# Revit family: Diverter-American_Standard-Townsend-T353.430.002
name_source: partatom
category: Plumbing Fixtures
revit_build: Autodesk Revit 2015 (Build: 20140606_1530(x64)
units: mm (PartAtom-declared; Revit-internal decimal feet)

## types (1)
- T353.430.002
    Assembly Code = D2020300
    CW Connection = Yes
    Cold Water Connection Diameter = 1/2"
    Cold Water Connection Radius = 1/4"
    Default Elevation = 40"
    Description = Townsend Diverter Valve Trim Kit
    Finish = Metal-American Standard-002-Chrome
    HW Connection = Yes
    Height = 3 13/16"
    Hot Water Connection Diameter = 1"
    Hot Water Connection Radius = 1/4"
    Installation Type = Wall Mounted
    Length = 3 1/16"
    Manufacturer = American Standard
    Material = Metal-American Standard-002-Chrome
    Model = T353.430.002
    Price = Prices may vary. Please consult Manufacturer Representative for most up-to-date price list.
    Product Documentation Link = https://www.americanstandard-us.com
    Product Page URL = https://www.americanstandard-us.com
    Tempered Water Connection Diameter = 1/2"
    Tempered Water Connection Radius = 1/4"
    URL = https://www.americanstandard-us.com
    Width = 2 5/16"

## geometry (parser evidence)
native form markers: Sweep x3
no freeform markers — native parametric forms only
